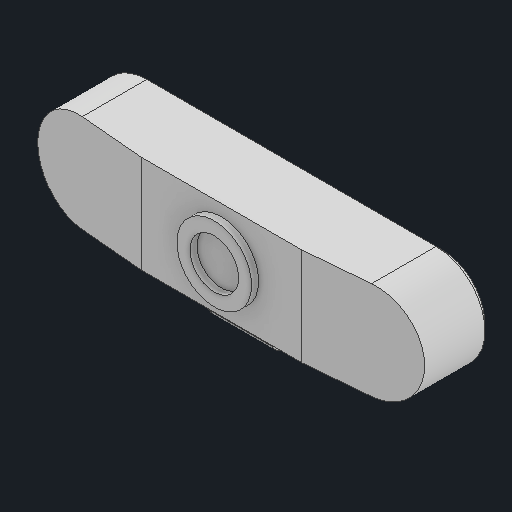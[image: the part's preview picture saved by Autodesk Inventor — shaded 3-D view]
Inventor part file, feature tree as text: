
AUTODESK INVENTOR PART (.ipt)
format: ipt  version: 2024 (Build 280153000, 153)  size: 149,504 bytes
history: native  units: in
note: dims shown in document units (in); Inventor stores cm internally (conversion verified against a paired STEP export)
features: extrude x4, sketch x3, chamfer x3
ambient origin geometry x8: Origin, YZ Plane, XZ Plane, XY Plane, X Axis, Y Axis, Z Axis, Center Point
bodies: Solid1 (feature_tree)
feature tree (10):
  sketch  "Sketch1"  dims[d0=4.8819in d1=1.2323in]
  extrude  "Extrusion1"  Depth=1.2323in
  extrude  "Extrusion2"  Depth=0.0886in
  chamfer  "Chamfer1"  Distance=0.0886in
  chamfer  "Chamfer2"  Distance=0.125in
  extrude  "Extrusion3"  Depth=0.9646in TaperAngle=0.0deg
  chamfer  "Chamfer3"  Distance=0.0787in
  extrude  "Extrusion4"  Depth=0.4173in
  sketch  "Sketch2"  dims[d2=0.9646in d3=0.0in d4=0.9429in d5=0.0886in d6=0.0in d8=0.125in d9=0.125in d10=0.5841in]
  sketch  "Sketch4"  dims[d11=0.125in d12=0.125in d13=0.5841in d14=0.9646in d15=0.0in d16=0.0787in d17=0.125in d18=0.5841in d19=0.4173in d20=0.3543in d21=0.3051in d22=0.1772in d23=0.0748in d24=0.7953in d25=0.0in]
